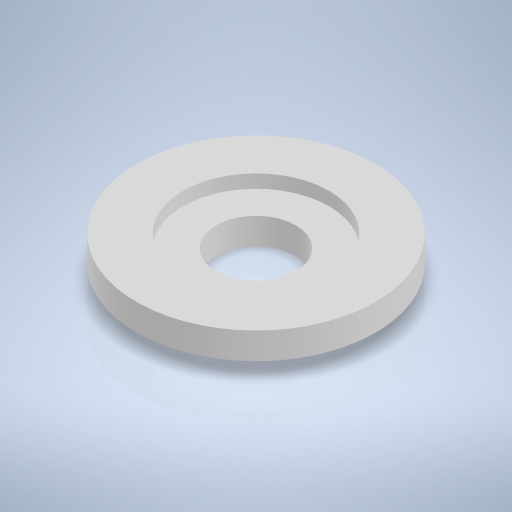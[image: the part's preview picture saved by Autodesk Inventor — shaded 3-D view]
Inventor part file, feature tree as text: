
AUTODESK INVENTOR PART (.ipt)
format: ipt  version: 2024 (Build 280153000, 153)  size: 246,784 bytes
history: native  units: mm
features: revolve x2, sketch x2
ambient origin geometry x8: Origin, YZ Plane, XZ Plane, XY Plane, X Axis, Y Axis, Z Axis, Center Point
bodies: Volumenkörper1 (feature_tree)
feature tree (4):
  revolve  "Umdrehung1"
  revolve  "Umdrehung2"
  sketch  "Skizze1"  dims[d0=1.5mm]
  sketch  "Skizze3"  dims[d1=0.5mm d2=9.0mm d3=7.0mm d4=90.0deg d5=3.0mm d6=5.5mm d7=0.5mm d8=90.0deg]
